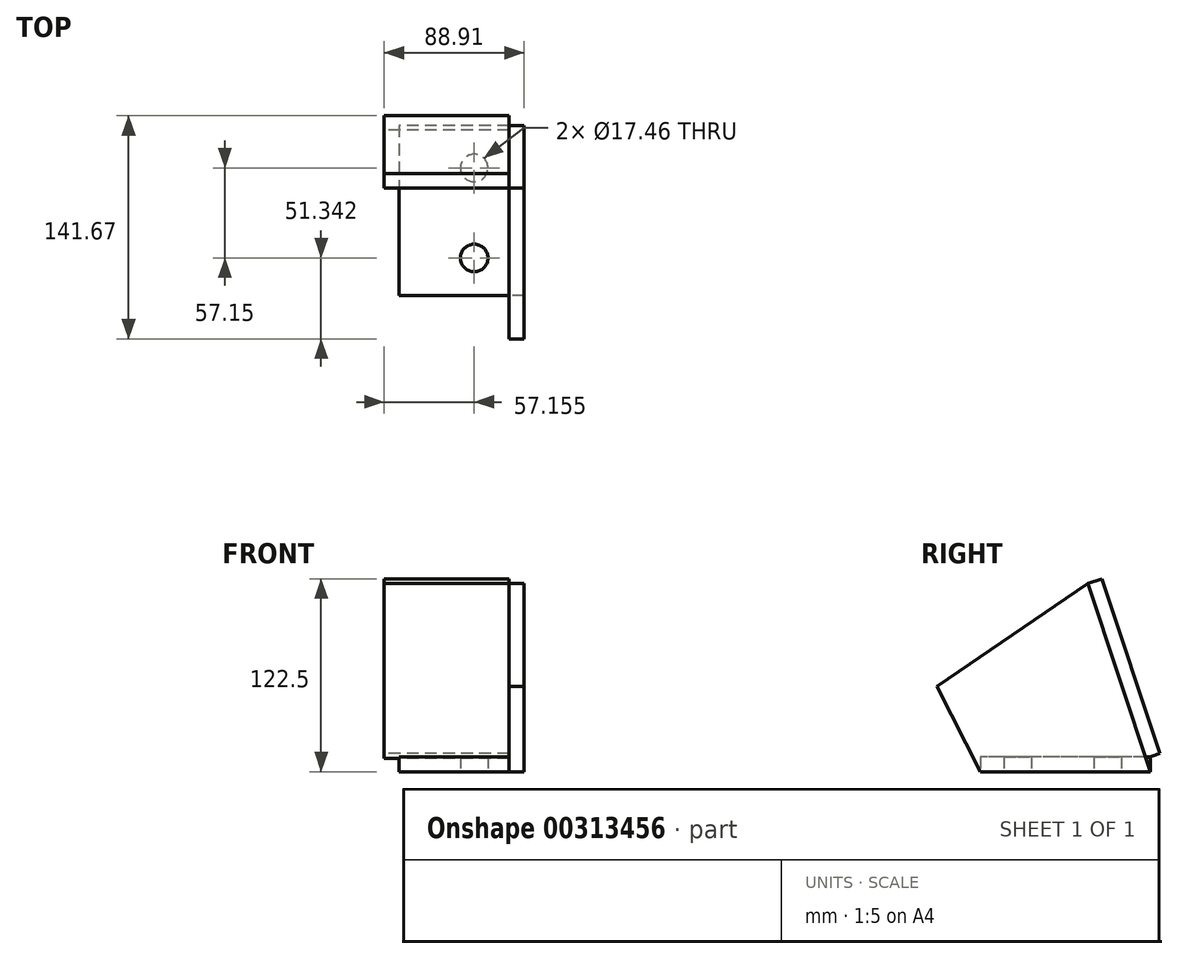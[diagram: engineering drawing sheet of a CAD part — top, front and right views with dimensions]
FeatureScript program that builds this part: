
annotation { "Feature Type Name" : "Feature", "Feature Type Description" : "" }
export const myFeature = defineFeature(function(context is Context, id is Id, definition is map)
    precondition{}
    {
        {
            var Q0;
            Q0=qCreatedBy(makeId("Right.planeOp"),FACE);
            var sketch = newSketch(context, id + "F0", { "sketchPlane" : qUnion([Q0])});
            skLineSegment(sketch, "E0", {"start": v(0, 0) * mm, "end": v(-107.95, 0) * mm});
            skLineSegment(sketch, "E1", {"start": v(-107.95, 0) * mm, "end": v(-135.48, 54.28) * mm});
            skLineSegment(sketch, "E2", {"start": v(-135.48, 54.28) * mm, "end": v(-39.69, 119.5) * mm});
            skLineSegment(sketch, "E3", {"start": v(-39.69, 119.5) * mm, "end": v(0, 0) * mm});
            skLineSegment(sketch, "E4", {"start": v(-39.69, 115.35) * mm, "end": v(-39.69, -58.98) * mm, "construction": true});
            skLineSegment(sketch, "E5", {"start": v(-107.95, 111.62) * mm, "end": v(-107.95, -42.93) * mm, "construction": true});
            skPoint(sketch, "E6", {"position": v(-107.95, 73.03) * mm});
            skSolve(sketch);
        }
        {
            var Q0;
            Q0=makeQuery(id+"F0.imprint","IMPRINT",FACE,{"disambiguationData":[TD([[makeQuery(id+"F0.imprint","IMPRINT",EDGE,{"derivedFrom":sQuery(id+"F0.wireOp",EDGE,"E0")}),-1.0]])]});
            extrude(context, id + "F1", {"entities" : qUnion([Q0]), "depth" : 9.52 * mm});
        }
        {
            var Q0;
            Q0=qCreatedBy(makeId("Top.planeOp"),FACE);
            var sketch = newSketch(context, id + "F2", { "sketchPlane" : qUnion([Q0])});
            skPoint(sketch, "E7.0", {"position": v(0, -107.95) * mm});
            skLineSegment(sketch, "E8.bottom", {"start": v(0, 0) * mm, "end": v(-69.85, 0) * mm});
            skLineSegment(sketch, "E8.top", {"start": v(0, -107.95) * mm, "end": v(-69.85, -107.95) * mm});
            skLineSegment(sketch, "E8.left", {"start": v(0, 0) * mm, "end": v(0, -107.95) * mm});
            skLineSegment(sketch, "E8.right", {"start": v(-69.85, 0) * mm, "end": v(-69.85, -107.95) * mm});
            skPoint(sketch, "E9.0", {"position": v(9.53, 0) * mm});
            skLineSegment(sketch, "E10", {"start": v(-22.23, 17) * mm, "end": v(-22.22, -151.62) * mm, "construction": true});
            skPoint(sketch, "E11", {"position": v(-22.22, -26.99) * mm});
            skPoint(sketch, "E12", {"position": v(-22.22, -84.14) * mm});
            skCircle(sketch, "E13", {"center": v(-22.22, -26.99) * mm, "radius": 8.73 * mm});
            skCircle(sketch, "E14", {"center": v(-22.22, -84.14) * mm, "radius": 8.73 * mm});
            skSolve(sketch);
        }
        {
            var Q0;
            Q0=makeQuery(id+"F2.imprint","IMPRINT",FACE,{"disambiguationData":[TD([[makeQuery(id+"F2.imprint","IMPRINT",EDGE,{"derivedFrom":sQuery(id+"F2.wireOp",EDGE,"E8.bottom")}),1.0]])]});
            extrude(context, id + "F3", {"entities" : qUnion([Q0]), "depth" : 9.52 * mm});
        }
        {
            var Q0;
            Q0=makeQuery(id+"F1.opExtrude","SWEPT_FACE",FACE,{"disambiguationData":[OSD([sQuery(id+"F0.wireOp",EDGE,"E3")])]});
            var sketch = newSketch(context, id + "F4", { "sketchPlane" : qUnion([Q0])});
            skLineSegment(sketch, "E15.0", {"start": v(-9.53, 125.91) * mm, "end": v(-9.53, 0) * mm});
            skLineSegment(sketch, "E16.0", {"start": v(0, 9.04) * mm, "end": v(69.85, 9.04) * mm});
            skLineSegment(sketch, "E17", {"start": v(-9.53, 125.91) * mm, "end": v(-9.53, 9.04) * mm});
            skLineSegment(sketch, "E18", {"start": v(-9.52, 9.04) * mm, "end": v(79.38, 9.04) * mm});
            skLineSegment(sketch, "E19", {"start": v(79.38, 9.04) * mm, "end": v(79.38, 125.91) * mm});
            skLineSegment(sketch, "E20", {"start": v(79.38, 125.91) * mm, "end": v(-9.52, 125.91) * mm});
            skSolve(sketch);
        }
        {
            var Q0;
            {var subQ0=sQuery(id+"F4.wireOp",EDGE,"E17");Q0=makeQuery(id+"F4.imprint","IMPRINT",FACE,{"disambiguationData":[TD([[makeQuery(id+"F4.imprint","IMPRINT",EDGE,{"derivedFrom":subQ0}),1.0]])]});}
            var Q1;
            {var subQ0=sQuery(id+"F4.wireOp",EDGE,"E19");Q1=makeQuery(id+"F4.imprint","IMPRINT",FACE,{"disambiguationData":[TD([[makeQuery(id+"F4.imprint","IMPRINT",EDGE,{"derivedFrom":subQ0}),1.0]])]});}
            extrude(context, id + "F5", {"entities" : qUnion([Q0, Q1]), "depth" : 9.52 * mm});
        }
    });
